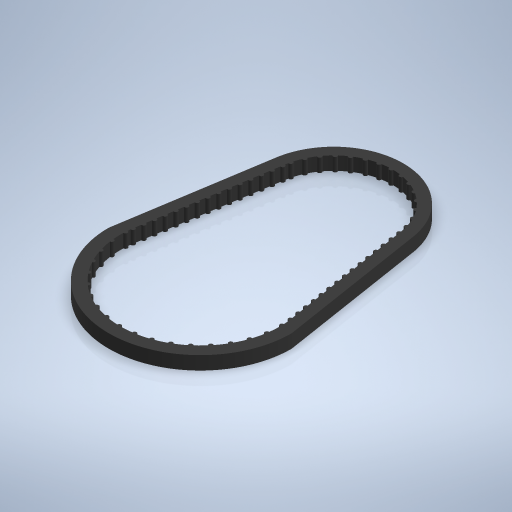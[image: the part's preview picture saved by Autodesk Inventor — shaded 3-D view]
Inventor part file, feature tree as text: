
AUTODESK INVENTOR PART (.ipt)
format: ipt  version: 2024 (Build 280153000, 153)  size: 502,784 bytes
history: native  units: mm
features: extrude x4, sketch x4, fillet x3, other x2, plane x2, pattern_circular x2, pattern_linear x1, mirror x1
ambient origin geometry x8: Origin, YZ Plane, XZ Plane, XY Plane, X Axis, Y Axis, Z Axis, Center Point
bodies: Body1 (feature_tree)
feature tree (19):
  extrude  "Extrusion2"  Depth=500.0mm
  extrude  "Extrusion3"  Depth=260.0mm
  fillet  "Rundung1"  Radius=50.0mm
  other  "Arbeitspunkt3"
  other  "Arbeitsachse3"
  pattern_linear  "Rechteckige Anordnung1"  Spacing1=7.5mm  [1 undecoded]
  plane  "Arbeitsebene1"
  mirror  "Spiegeln4"
  fillet  "Rundung2"  Radius=35.0mm
  fillet  "Rundung3"  [1 undecoded]
  plane  "Arbeitsebene3"
  extrude  "Extrusion5"  Depth=50.0mm
  pattern_circular  "Runde Anordnung2"  Count=5  [1 undecoded]
  extrude  "Extrusion6"  TaperAngle=0.0deg  [1 undecoded]
  pattern_circular  "Runde Anordnung3"  [2 undecoded]
  sketch  "Skizze1"  dims[d0=500.0mm d1=3.141593mm]
  sketch  "Skizze2"  dims[d2=220.0mm d5=260.0mm d6=50.0mm d7=0.0mm]
  sketch  "Skizze4"  dims[d9=15.0mm]
  sketch  "Skizze5"  dims[d10=8.0mm d11=0.0mm d12=7.5mm d13=150.0mm d15=35.0mm d19=0.0mm d21=50.0mm d22=50.0mm d28=0.0mm d29=35.0mm d30=7.5mm d31=8.0mm d32=0.0mm d33=150.0mm d34=150.0deg d36=7.5mm d37=35.0mm d38=10.0mm d39=0.0mm d40=190.0mm d41=32.288591mm]
note: 6 required parameter values undecoded (feature->parameter linkage not recoverable at this tier; creation-order binding heuristic only, values carry confidence <= 0.55)
